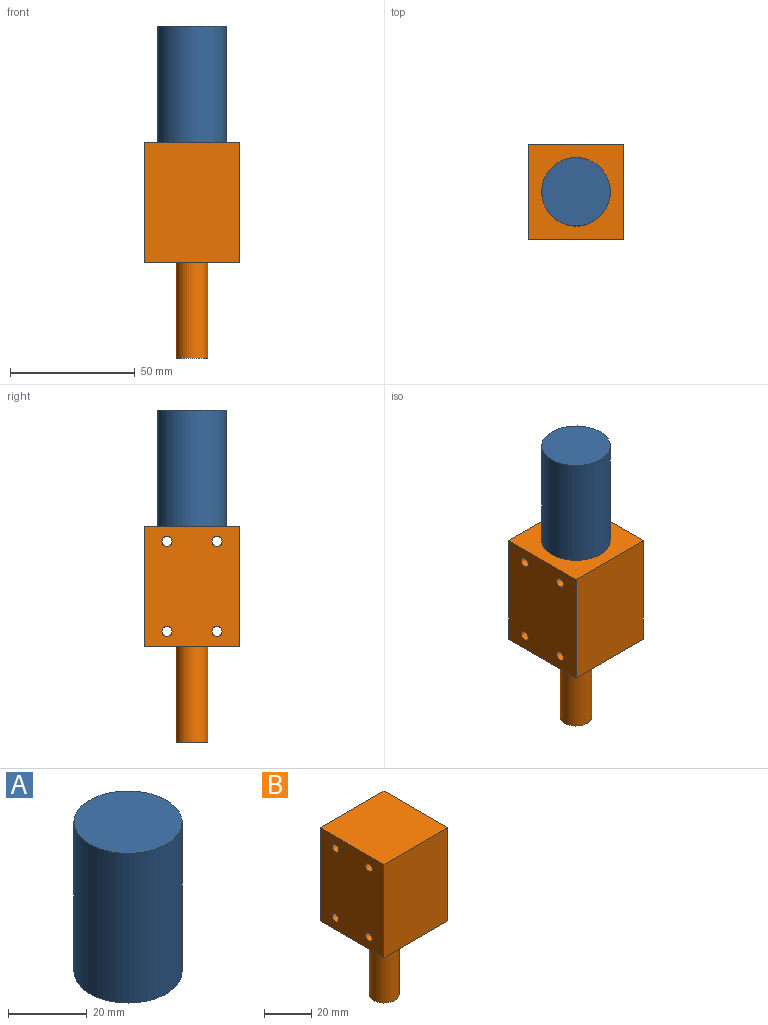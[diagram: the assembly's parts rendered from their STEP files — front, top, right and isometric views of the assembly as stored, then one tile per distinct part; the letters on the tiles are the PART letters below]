
ASSEMBLY  parts=2 mates=1
PART A: 3 faces, bbox 27.4x27.4x46.5 mm
  f0: cylinder r=13.72mm len=46.48mm, axis (0,0,-1), area 4005.8mm2, adj f1,f2
  f1: plane 27.43x27.43mm, normal (0,0,1), area 591mm2, adj f0
  f2: plane 27.43x27.43mm, normal (0,0,-1), area 591mm2, adj f0
PART B: 12 faces, bbox 38.1x38.1x86.4 mm
  f0: plane 48.26x38.1mm, normal (0,1,0), area 1838.7mm2, adj f1,f3,f4,f5
  f1: plane 48.26x38.1mm, normal (-1,0,0), area 1787.5mm2, adj f0,f2,f4,f5,f6,f7,f8,f9
  f2: plane 48.26x38.1mm, normal (0,-1,0), area 1838.7mm2, adj f1,f3,f4,f5
  f3: plane 48.26x38.1mm, normal (1,0,0), area 1787.5mm2, adj f0,f2,f4,f5,f6,f7,f8,f9
  f4: plane 38.1x38.1mm, normal (0,0,1), area 1451.6mm2, adj f0,f1,f2,f3
  f5: plane 38.1x38.1mm, normal (0,0,-1), area 1324.9mm2, adj f0,f1,f2,f3,f10
  f6: cylinder r=2.02mm len=38.1mm, axis (1,0,0), area 483.4mm2, adj f1,f3
  f7: cylinder r=2.02mm len=38.1mm, axis (1,0,0), area 483.4mm2, adj f1,f3
  f8: cylinder r=2.02mm len=38.1mm, axis (1,0,0), area 483.4mm2, adj f1,f3
  f9: cylinder r=2.02mm len=38.1mm, axis (1,0,0), area 483.4mm2, adj f1,f3
  f10: cylinder r=6.35mm len=38.1mm, axis (0,0,1), area 1520.1mm2, adj f5,f11
  f11: plane 12.7x12.7mm, normal (0,0,-1), area 126.7mm2, adj f10
PLACE A t=(13.5,0,66)mm
PLACE B t=(13.5,0,17.74)mm
MATE fastened B.f10 <-> A.f0  axis (0,0,1) through (13.5,0,66)mm
